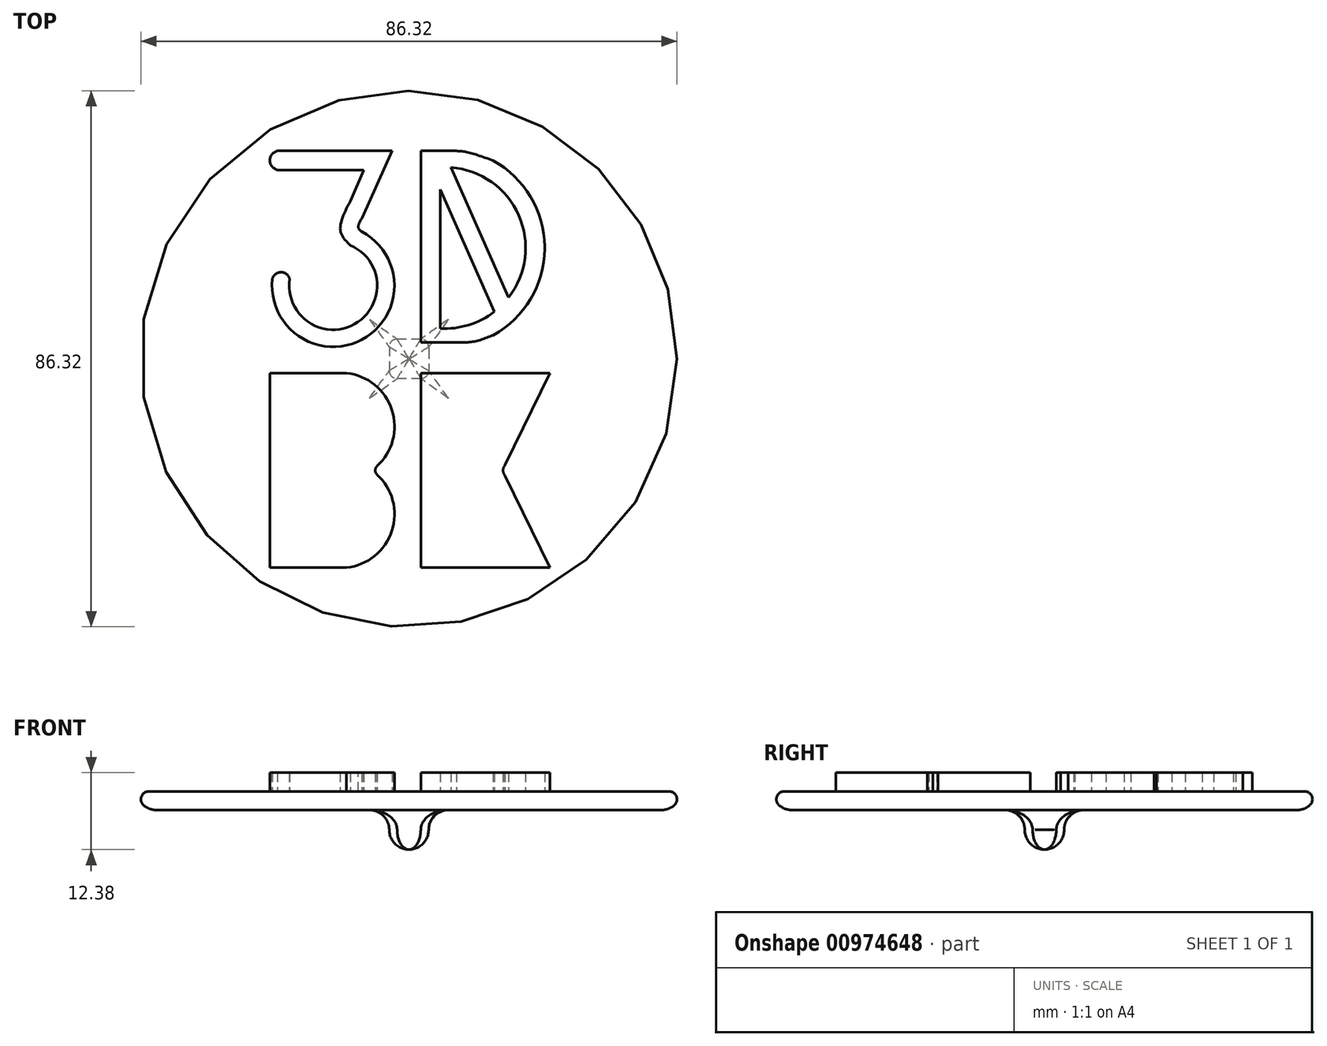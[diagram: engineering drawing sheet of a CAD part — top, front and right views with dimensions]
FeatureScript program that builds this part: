
annotation { "Feature Type Name" : "Feature", "Feature Type Description" : "" }
export const myFeature = defineFeature(function(context is Context, id is Id, definition is map)
    precondition{}
    {
        {
            var Q0;
            Q0=qCreatedBy(makeId("Top.planeOp"),FACE);
            var sketch = newSketch(context, id + "F0", { "sketchPlane" : qUnion([Q0])});
            skLineSegment(sketch, "E0", {"start": v(0, 56.35) * mm, "end": v(0, -56.35) * mm});
            skLineSegment(sketch, "E1", {"start": v(56.35, 0) * mm, "end": v(-56.35, 0) * mm});
            skPoint(sketch, "E2", {"position": v(0, 0) * mm});
            skPoint(sketch, "E3", {"position": v(-22.39, -33.62) * mm});
            skPoint(sketch, "E4", {"position": v(-22.39, 33.48) * mm});
            skPoint(sketch, "E5", {"position": v(21.85, 33.48) * mm});
            skLineSegment(sketch, "E6", {"start": v(1.95, 33.48) * mm, "end": v(7.67, 33.48) * mm});
            skLineSegment(sketch, "E7", {"start": v(21.85, -33.62) * mm, "end": v(1.95, -33.62) * mm});
            skLineSegment(sketch, "E8", {"start": v(21.85, 18.05) * mm, "end": v(21.85, 17.68) * mm});
            skLineSegment(sketch, "E9", {"start": v(-2.74, 33.48) * mm, "end": v(-21.16, 33.48) * mm});
            skLineSegment(sketch, "E10", {"start": v(-22.39, -33.62) * mm, "end": v(-10.07, -33.62) * mm});
            skLineSegment(sketch, "E11", {"start": v(-22.39, -2.3) * mm, "end": v(-22.39, -33.62) * mm});
            skPoint(sketch, "E12", {"position": v(-22.39, 31.95) * mm});
            skPoint(sketch, "E12.positionSnap0", {"position": v(-21.16, 31.95) * mm});
            skArc(sketch, "E13", {"start": v(-21.16, 33.48) * mm, "mid": v(-22.39, 31.95) * mm, "end": v(-21.16, 30.43) * mm});
            skPoint(sketch, "E14", {"position": v(-2.74, 33.48) * mm});
            skPoint(sketch, "E15", {"position": v(-7.3, 30.43) * mm});
            skLineSegment(sketch, "E16", {"start": v(-21.16, 30.43) * mm, "end": v(-7.3, 30.43) * mm});
            skPoint(sketch, "E17", {"position": v(-11.04, 20.68) * mm});
            skPoint(sketch, "E18", {"position": v(-9.45, 18.3) * mm});
            skPoint(sketch, "E19", {"position": v(-9.45, 25.39) * mm});
            skFitSpline(sketch, "E20", {"points": [v(-9.45, 25.39) * mm, v(-11.04, 20.68) * mm, v(-9.45, 18.3) * mm], "startDerivative": vector(-4.65, -9.06) * mm, "endDerivative": vector(5.1, -4.94) * mm});
            skLineSegment(sketch, "E21", {"start": v(-7.3, 30.43) * mm, "end": v(-9.45, 25.39) * mm});
            skPoint(sketch, "E22", {"position": v(-19.2, 12.85) * mm});
            skPoint(sketch, "E23", {"position": v(-12.14, 4.7) * mm});
            skArc(sketch, "E24", {"start": v(-19.2, 12.85) * mm, "mid": v(-8.74, 5.6) * mm, "end": v(-9.45, 18.3) * mm});
            skPoint(sketch, "E25", {"position": v(-8.14, 21.15) * mm});
            skPoint(sketch, "E26", {"position": v(-7.55, 20.43) * mm});
            skPoint(sketch, "E27", {"position": v(-7.55, 22.7) * mm});
            skFitSpline(sketch, "E28", {"points": [v(-7.55, 22.7) * mm, v(-8.14, 21.15) * mm, v(-7.55, 20.43) * mm], "startDerivative": vector(-1.74, -3) * mm, "endDerivative": vector(1.9, -1.47) * mm});
            skLineSegment(sketch, "E29", {"start": v(-2.74, 33.48) * mm, "end": v(-7.55, 22.7) * mm});
            skArc(sketch, "E30.0", {"start": v(-21.98, 12.85) * mm, "mid": v(-7.57, 3.08) * mm, "end": v(-7.62, 20.5) * mm});
            skPoint(sketch, "E31", {"position": v(-21.98, 12.85) * mm});
            skPoint(sketch, "E32", {"position": v(-20.63, 13.93) * mm});
            skArc(sketch, "E33", {"start": v(-19.2, 12.85) * mm, "mid": v(-20.59, 13.94) * mm, "end": v(-21.98, 12.85) * mm});
            skLineSegment(sketch, "E34", {"start": v(1.95, 33.48) * mm, "end": v(1.95, 2.25) * mm});
            skPoint(sketch, "E35", {"position": v(21.85, 18.05) * mm});
            skArc(sketch, "E36", {"start": v(13.56, 3.8) * mm, "mid": v(21.85, 17.87) * mm, "end": v(13.56, 31.93) * mm});
            skPoint(sketch, "E37", {"position": v(7.67, 33.48) * mm});
            skPoint(sketch, "E38", {"position": v(13.56, 31.93) * mm});
            skPoint(sketch, "E39", {"position": v(13.56, 3.8) * mm});
            skArc(sketch, "E40.0", {"start": v(5.03, 4.88) * mm, "mid": v(9.62, 5.44) * mm, "end": v(13.73, 7.58) * mm});
            skLineSegment(sketch, "E40.1", {"start": v(5.03, 27.26) * mm, "end": v(5.03, 4.88) * mm});
            skLineSegment(sketch, "E41", {"start": v(5.03, 27.26) * mm, "end": v(13.73, 7.58) * mm});
            skLineSegment(sketch, "E42", {"start": v(16.04, 9.89) * mm, "end": v(6.78, 30.83) * mm});
            skLineSegment(sketch, "E43", {"start": v(-22.39, -2.3) * mm, "end": v(-10.07, -2.3) * mm});
            skLineSegment(sketch, "E44", {"start": v(1.95, -2.3) * mm, "end": v(1.95, -33.62) * mm});
            skLineSegment(sketch, "E45", {"start": v(1.95, -2.3) * mm, "end": v(22.67, -2.3) * mm});
            skLineSegment(sketch, "E46", {"start": v(22.67, -2.3) * mm, "end": v(15.49, -17.1) * mm});
            skFitSpline(sketch, "E47", {"points": [v(15.49, -17.1) * mm, v(15.2, -17.6) * mm, v(15.17, -17.96) * mm], "startDerivative": vector(-0.63, -0.9) * mm, "endDerivative": vector(0.03, -0.82) * mm});
            skLineSegment(sketch, "E48.MirrorCS", {"start": v(1.95, -33.62) * mm, "end": v(22.67, -33.62) * mm});
            skLineSegment(sketch, "E49.MirrorCS", {"start": v(22.67, -33.62) * mm, "end": v(15.49, -18.82) * mm});
            skFitSpline(sketch, "E50.MirrorCS", {"points": [v(15.49, -18.82) * mm, v(15.2, -18.34) * mm, v(15.17, -17.96) * mm], "startDerivative": vector(-0.63, 0.9) * mm, "endDerivative": vector(0.03, 0.82) * mm});
            skArc(sketch, "E51", {"start": v(-5.17, -17.31) * mm, "mid": v(-2.75, -8.22) * mm, "end": v(-10.07, -2.3) * mm});
            skFitSpline(sketch, "E52", {"points": [v(-5.17, -17.31) * mm, v(-5.38, -17.68) * mm, v(-5.4, -17.96) * mm], "startDerivative": vector(-0.48, -0.68) * mm, "endDerivative": vector(0.02, -0.62) * mm});
            skArc(sketch, "E53.MirrorCS", {"start": v(-5.17, -18.61) * mm, "mid": v(-2.75, -27.7) * mm, "end": v(-10.07, -33.62) * mm});
            skFitSpline(sketch, "E54.MirrorCS", {"points": [v(-5.17, -18.61) * mm, v(-5.38, -18.25) * mm, v(-5.4, -17.96) * mm], "startDerivative": vector(-0.48, 0.68) * mm, "endDerivative": vector(0.02, 0.62) * mm});
            skPoint(sketch, "E55.end.orphan", {"position": v(-10.07, -33.62) * mm});
            skPoint(sketch, "E56.orphan", {"position": v(-10.07, -17.96) * mm});
            skPoint(sketch, "E57.orphan", {"position": v(0, -33.62) * mm});
            skLineSegment(sketch, "E58.MirrorCS", {"start": v(0, 2.62) * mm, "end": v(7.67, 2.62) * mm});
            skArc(sketch, "E59.trimOffspring", {"start": v(16.04, 9.89) * mm, "mid": v(17.67, 23.12) * mm, "end": v(6.78, 30.83) * mm});
            skPoint(sketch, "E60", {"position": v(7.67, 2.62) * mm});
            skFitSpline(sketch, "E61", {"points": [v(13.56, 3.8) * mm, v(10.55, 2.81) * mm, v(7.67, 2.62) * mm], "startDerivative": vector(-5.9, -2.33) * mm, "endDerivative": vector(-5.9, -0.02) * mm});
            skPoint(sketch, "E62.1.internal.snap0", {"position": v(9.38, 17.42) * mm});
            skFitSpline(sketch, "E62", {"points": [v(13.56, 31.93) * mm, v(9.38, 33.27) * mm, v(7.67, 33.48) * mm], "startDerivative": vector(-7.54, 2.7) * mm, "endDerivative": vector(-3.99, 0.22) * mm});
            skPoint(sketch, "E63.orphan", {"position": v(10.87, 2.62) * mm});
            skPoint(sketch, "E64.orphan", {"position": v(0, 33.48) * mm});
            skPoint(sketch, "E65.trimOffspring.start.orphan", {"position": v(21.85, 2.62) * mm});
            skLineSegment(sketch, "E66", {"start": v(-27.8, 0) * mm, "end": v(-27.8, 46.45) * mm});
            skLineSegment(sketch, "E67", {"start": v(-27.8, 46.45) * mm, "end": v(0, 46.45) * mm});
            skLineSegment(sketch, "E68.MirrorCS", {"start": v(27.8, 0) * mm, "end": v(27.8, 46.45) * mm});
            skLineSegment(sketch, "E69.MirrorCS", {"start": v(-27.8, -46.45) * mm, "end": v(0, -46.45) * mm});
            skLineSegment(sketch, "E70.MirrorCS", {"start": v(-27.8, 0) * mm, "end": v(-27.8, -46.45) * mm});
            skLineSegment(sketch, "E71.MirrorCS", {"start": v(27.8, 46.45) * mm, "end": v(0, 46.45) * mm});
            skLineSegment(sketch, "E72.MirrorCS", {"start": v(27.8, 0) * mm, "end": v(27.8, -46.45) * mm});
            skLineSegment(sketch, "E73.MirrorCS", {"start": v(27.8, -46.45) * mm, "end": v(0, -46.45) * mm});
            skSolve(sketch);
        }
        {
            var Q0;
            Q0=qCreatedBy(makeId("Top.planeOp"),FACE);
            var sketch = newSketch(context, id + "F1", { "sketchPlane" : qUnion([Q0])});
            skCircle(sketch, "E74", {"center": v(0, 0) * mm, "radius": 43.82 * mm});
            skSolve(sketch);
        }
        {
            var Q0;
            Q0 = qSketchRegion(id + "F1", true);
            extrude(context, id + "F2", {"entities" : qUnion([Q0]), "oppositeDirection" : true, "depth" : 3 * mm, "offsetDistance" : 25.4 * mm});
        }
        {
            var Q0;
            Q0=makeQuery(id+"F0.imprint","IMPRINT",FACE,{"disambiguationData":[TD([[makeQuery(id+"F0.imprint","IMPRINT",EDGE,{"derivedFrom":sQuery(id+"F0.wireOp",EDGE,"E10")}),1.0]])]});
            var Q1;
            {var subQ0=sQuery(id+"F0.wireOp",EDGE,"E44");Q1=makeQuery(id+"F0.imprint","IMPRINT",FACE,{"disambiguationData":[TD([[makeQuery(id+"F0.imprint","IMPRINT",EDGE,{"derivedFrom":subQ0}),1.0]])]});}
            var Q2;
            Q2=makeQuery(id+"F0.imprint","IMPRINT",FACE,{"disambiguationData":[TD([[makeQuery(id+"F0.imprint","IMPRINT",EDGE,{"derivedFrom":sQuery(id+"F0.wireOp",EDGE,"E9")}),1.0]])]});
            var Q3;
            {var subQ7=sQuery(id+"F0.wireOp",EDGE,"E6");Q3=makeQuery(id+"F0.imprint","IMPRINT",FACE,{"disambiguationData":[TD([[makeQuery(id+"F0.imprint","IMPRINT",EDGE,{"derivedFrom":subQ7}),-1.0]])]});}
            extrude(context, id + "F3", {"entities" : qUnion([Q0, Q1, Q2, Q3]), "operationType" : NewBodyOperationType.ADD, "depth" : 3 * mm, "offsetDistance" : 25.4 * mm});
        }
        {
            var Q0;
            Q0=makeQuery(id+"F2.opExtrude","CAP_FACE",FACE,{"disambiguationData":[OSD([sQuery(id+"F1.wireOp",EDGE,"E74")])],"isStart":false});
            var sketch = newSketch(context, id + "F4", { "sketchPlane" : qUnion([Q0])});
            skLineSegment(sketch, "E75.bottom", {"start": v(3.18, -3.17) * mm, "end": v(-3.18, -3.18) * mm});
            skLineSegment(sketch, "E75.top", {"start": v(3.18, 3.18) * mm, "end": v(-3.18, 3.17) * mm});
            skLineSegment(sketch, "E75.left", {"start": v(3.18, -3.17) * mm, "end": v(3.18, 3.18) * mm});
            skLineSegment(sketch, "E75.right", {"start": v(-3.18, -3.18) * mm, "end": v(-3.18, 3.17) * mm});
            skPoint(sketch, "E75.middle", {"position": v(0, 0) * mm});
            skSolve(sketch);
        }
        {
            var Q0;
            Q0 = qSketchRegion(id + "F4", true);
            extrude(context, id + "F5", {"entities" : qUnion([Q0]), "operationType" : NewBodyOperationType.ADD, "depth" : 6.38 * mm, "offsetDistance" : 25.4 * mm});
        }
        {
            var Q0;
            Q0=makeQuery(id+"F5.opExtrude","CAP_EDGE",EDGE,{"disambiguationData":[OSD([sQuery(id+"F4.wireOp",EDGE,"E75.right")])],"isStart":false});
            var Q1;
            Q1=makeQuery(id+"F5.opExtrude","CAP_EDGE",EDGE,{"disambiguationData":[OSD([sQuery(id+"F4.wireOp",EDGE,"E75.top")])],"isStart":false});
            var Q2;
            Q2=makeQuery(id+"F5.opExtrude","CAP_EDGE",EDGE,{"disambiguationData":[OSD([sQuery(id+"F4.wireOp",EDGE,"E75.left")])],"isStart":false});
            var Q3;
            Q3=makeQuery(id+"F5.opExtrude","CAP_EDGE",EDGE,{"disambiguationData":[OSD([sQuery(id+"F4.wireOp",EDGE,"E75.bottom")])],"isStart":false});
            var Q4;
            Q4=makeQuery(id+"F5.opExtrude","CAP_EDGE",EDGE,{"disambiguationData":[OSD([sQuery(id+"F4.wireOp",EDGE,"E75.right")])],"isStart":true});
            var Q5;
            Q5=makeQuery(id+"F5.opExtrude","CAP_EDGE",EDGE,{"disambiguationData":[OSD([sQuery(id+"F4.wireOp",EDGE,"E75.top")])],"isStart":true});
            var Q6;
            Q6=makeQuery(id+"F5.opExtrude","CAP_EDGE",EDGE,{"disambiguationData":[OSD([sQuery(id+"F4.wireOp",EDGE,"E75.bottom")])],"isStart":true});
            var Q7;
            Q7=makeQuery(id+"F5.opExtrude","CAP_EDGE",EDGE,{"disambiguationData":[OSD([sQuery(id+"F4.wireOp",EDGE,"E75.left")])],"isStart":true});
            var Q8;
            Q8=makeQuery(id+"F2.opExtrude","CAP_FACE",FACE,{"disambiguationData":[OSD([sQuery(id+"F1.wireOp",EDGE,"E74")])],"isStart":false});
            fillet(context, id + "F6", {"entities" : qUnion([Q0, Q1, Q2, Q3, Q4, Q5, Q6, Q7, Q8]), "radius" : 3.17 * mm, "tangentPropagation" : true, "allowEdgeOverflow" : false});
        }
        {
            var Q0;
            Q0=makeQuery(id+"F5.opExtrude","SWEPT_FACE",FACE,{"disambiguationData":[OSD([sQuery(id+"F4.wireOp",EDGE,"E75.left")])]});
            extrude(context, id + "F7", {"entities" : qUnion([Q0]), "operationType" : NewBodyOperationType.ADD, "depth" : 25.4 * mm, "offsetDistance" : 25.4 * mm});
        }
        {
            var Q0;
            Q0=makeQuery(id+"F7.opExtrude","CAP_FACE",FACE,{"disambiguationData":[OSD([sQuery(id+"F4.wireOp",EDGE,"E75.left")])],"isStart":false});
            var sketch = newSketch(context, id + "F8", { "sketchPlane" : qUnion([Q0])});
            skCircle(sketch, "E76", {"center": v(0, -6.19) * mm, "radius": 1.5 * mm});
            skPoint(sketch, "E76.centerSnap0", {"position": v(3.17, -6.19) * mm});
            skPoint(sketch, "E76.centerSnap1", {"position": v(0, -6.2) * mm});
            skSolve(sketch);
        }
        {
            var Q0;
            {var subQ0=sQuery(id+"F8.wireOp",EDGE,"E76");var subQ1=sQuery(id+"F4.wireOp",EDGE,"E75.left");var subQ2=makeQuery(id+"F7.opExtrude","CAP_EDGE",EDGE,{"disambiguationData":[OSD([subQ1]),TDD([makeQuery(id+"F6.opFillet","BLEND_EDGE",EDGE,{"blendedFrom":[makeQuery(id+"F5.opExtrude","CAP_EDGE",EDGE,{"disambiguationData":[OSD([subQ1])],"isStart":true}),makeQuery(id+"F5.opExtrude","SWEPT_FACE",FACE,{"disambiguationData":[OSD([subQ1])]})],"blendedInto":[makeQuery(id+"F5.opExtrude","SWEPT_FACE",FACE,{"disambiguationData":[OSD([subQ1])]})]})])],"isStart":false});var subQ3=makeQuery(id+"F8.imprint","INTERSECT",VERTEX,{"disambiguationData":[OD(0.0)],"derivedFrom":[subQ2,subQ0]});Q0=makeQuery(id+"F8.imprint","IMPRINT",FACE,{"disambiguationData":[TD([[makeQuery(id+"F8.imprint","IMPRINT",EDGE,{"disambiguationData":[TD([[subQ3,1.0]])],"derivedFrom":subQ0}),1.0]])]});}
            var Q1;
            {var subQ0=sQuery(id+"F8.wireOp",EDGE,"E76");var subQ1=sQuery(id+"F4.wireOp",EDGE,"E75.left");var subQ2=makeQuery(id+"F7.opExtrude","CAP_EDGE",EDGE,{"disambiguationData":[OSD([subQ1]),TDD([makeQuery(id+"F6.opFillet","BLEND_EDGE",EDGE,{"blendedFrom":[makeQuery(id+"F5.opExtrude","CAP_EDGE",EDGE,{"disambiguationData":[OSD([subQ1])],"isStart":false}),makeQuery(id+"F5.opExtrude","SWEPT_FACE",FACE,{"disambiguationData":[OSD([subQ1])]})],"blendedInto":[makeQuery(id+"F5.opExtrude","SWEPT_FACE",FACE,{"disambiguationData":[OSD([subQ1])]})]})])],"isStart":false});var subQ3=makeQuery(id+"F8.imprint","INTERSECT",VERTEX,{"disambiguationData":[OD(0.0)],"derivedFrom":[subQ2,subQ0]});Q1=makeQuery(id+"F8.imprint","IMPRINT",FACE,{"disambiguationData":[TD([[makeQuery(id+"F8.imprint","IMPRINT",EDGE,{"disambiguationData":[TD([[subQ3,-1.0]])],"derivedFrom":subQ0}),1.0]])]});}
            var Q2;
            {var subQ0=sQuery(id+"F8.wireOp",EDGE,"E76");var subQ1=sQuery(id+"F4.wireOp",EDGE,"E75.left");var subQ2=makeQuery(id+"F5.opExtrude","SWEPT_FACE",FACE,{"disambiguationData":[OSD([subQ1])]});var subQ3=makeQuery(id+"F7.opExtrude","CAP_EDGE",EDGE,{"disambiguationData":[OSD([subQ1]),TDD([makeQuery(id+"F6.opFillet","BLEND_EDGE",EDGE,{"blendedFrom":[makeQuery(id+"F5.opExtrude","CAP_EDGE",EDGE,{"disambiguationData":[OSD([subQ1])],"isStart":true}),subQ2],"blendedInto":[subQ2]})])],"isStart":false});var subQ4=makeQuery(id+"F8.imprint","INTERSECT",VERTEX,{"disambiguationData":[OD(0.0)],"derivedFrom":[subQ3,subQ0]});Q2=makeQuery(id+"F8.imprint","IMPRINT",FACE,{"disambiguationData":[TD([[makeQuery(id+"F8.imprint","IMPRINT",EDGE,{"disambiguationData":[TD([[subQ4,-1.0]])],"derivedFrom":subQ0}),1.0]])]});}
            var Q3;
            {var subQ0=sQuery(id+"F4.wireOp",EDGE,"E75.right");Q3=makeQuery(id+"F6.opFillet","BLEND_FACE",FACE,{"disambiguationData":[OSD([subQ0]),TDD([makeQuery(id+"F5.opExtrude","CAP_EDGE",EDGE,{"disambiguationData":[OSD([subQ0])],"isStart":true})])]});}
            extrude(context, id + "F9", {"entities" : qUnion([Q0, Q1, Q2]), "operationType" : NewBodyOperationType.REMOVE, "endBound" : BoundingType.UP_TO_SURFACE, "oppositeDirection" : true, "depth" : 25.4 * mm, "endBoundEntityFace" : qUnion([Q3]), "offsetDistance" : 25.4 * mm});
        }
        {
            var Q0;
            {var subQ0=sQuery(id+"F4.wireOp",EDGE,"E75.left");var subQ2=sQuery(id+"F4.wireOp",EDGE,"E75.top");Q0=makeQuery(id+"F9.boolean.opBoolean","SPLIT",FACE,{"disambiguationData":[TD([makeQuery(id+"F5.opExtrude","SWEPT_FACE",FACE,{"disambiguationData":[OSD([subQ2])]})])],"derivedFrom":makeQuery(id+"F7.opExtrude","CAP_FACE",FACE,{"disambiguationData":[OSD([subQ0])],"isStart":false})});}
            var Q1;
            {var subQ0=sQuery(id+"F4.wireOp",EDGE,"E75.left");var subQ2=sQuery(id+"F4.wireOp",EDGE,"E75.bottom");Q1=makeQuery(id+"F9.boolean.opBoolean","SPLIT",FACE,{"disambiguationData":[TD([makeQuery(id+"F5.opExtrude","SWEPT_FACE",FACE,{"disambiguationData":[OSD([subQ2])]})])],"derivedFrom":makeQuery(id+"F7.opExtrude","CAP_FACE",FACE,{"disambiguationData":[OSD([subQ0])],"isStart":false})});}
            extrude(context, id + "F10", {"entities" : qUnion([Q0, Q1]), "operationType" : NewBodyOperationType.REMOVE, "oppositeDirection" : true, "depth" : 25.4 * mm, "offsetDistance" : 25.4 * mm});
        }
        {
            var Q0;
            {var subQ3=sQuery(id+"F1.wireOp",EDGE,"E74");Q0=makeQuery(id+"F6.opFillet","BLEND_EDGE",EDGE,{"blendedFrom":[makeQuery(id+"F2.opExtrude","CAP_EDGE",EDGE,{"disambiguationData":[OSD([subQ3])],"isStart":false}),makeQuery(id+"F3.boolean.opBoolean","SPLIT",FACE,{"disambiguationData":[TD([makeQuery(id+"F2.opExtrude","SWEPT_FACE",FACE,{"disambiguationData":[OSD([subQ3])]})])],"derivedFrom":makeQuery(id+"F2.opExtrude","CAP_FACE",FACE,{"disambiguationData":[OSD([subQ3])],"isStart":true})})],"blendedInto":[makeQuery(id+"F3.boolean.opBoolean","SPLIT",FACE,{"disambiguationData":[TD([makeQuery(id+"F2.opExtrude","SWEPT_FACE",FACE,{"disambiguationData":[OSD([subQ3])]})])],"derivedFrom":makeQuery(id+"F2.opExtrude","CAP_FACE",FACE,{"disambiguationData":[OSD([subQ3])],"isStart":true})})]});}
            fillet(context, id + "F11", {"entities" : qUnion([Q0]), "radius" : 1.27 * mm, "tangentPropagation" : true, "allowEdgeOverflow" : false});
        }
        {
            var Q0;
            Q0=makeQuery(id+"F6.opFillet","BLEND_EDGE",EDGE,{"blendedFrom":[makeQuery(id+"F5.opExtrude","CAP_EDGE",EDGE,{"disambiguationData":[OSD([sQuery(id+"F4.wireOp",EDGE,"E75.top")])],"isStart":false}),makeQuery(id+"F5.opExtrude","CAP_EDGE",EDGE,{"disambiguationData":[OSD([sQuery(id+"F4.wireOp",EDGE,"E75.left")])],"isStart":false})],"blendedInto":[]});
            var Q1;
            Q1=makeQuery(id+"F6.opFillet","BLEND_EDGE",EDGE,{"blendedFrom":[makeQuery(id+"F5.opExtrude","CAP_EDGE",EDGE,{"disambiguationData":[OSD([sQuery(id+"F4.wireOp",EDGE,"E75.bottom")])],"isStart":false}),makeQuery(id+"F5.opExtrude","CAP_EDGE",EDGE,{"disambiguationData":[OSD([sQuery(id+"F4.wireOp",EDGE,"E75.left")])],"isStart":false})],"blendedInto":[]});
            var Q2;
            Q2=makeQuery(id+"F6.opFillet","BLEND_EDGE",EDGE,{"blendedFrom":[makeQuery(id+"F5.opExtrude","CAP_EDGE",EDGE,{"disambiguationData":[OSD([sQuery(id+"F4.wireOp",EDGE,"E75.bottom")])],"isStart":false}),makeQuery(id+"F5.opExtrude","CAP_EDGE",EDGE,{"disambiguationData":[OSD([sQuery(id+"F4.wireOp",EDGE,"E75.right")])],"isStart":false})],"blendedInto":[]});
            var Q3;
            Q3=makeQuery(id+"F6.opFillet","BLEND_EDGE",EDGE,{"blendedFrom":[makeQuery(id+"F5.opExtrude","CAP_EDGE",EDGE,{"disambiguationData":[OSD([sQuery(id+"F4.wireOp",EDGE,"E75.top")])],"isStart":false}),makeQuery(id+"F5.opExtrude","CAP_EDGE",EDGE,{"disambiguationData":[OSD([sQuery(id+"F4.wireOp",EDGE,"E75.right")])],"isStart":false})],"blendedInto":[]});
            var Q4;
            Q4=makeQuery(id+"F2.opExtrude","CAP_FACE",FACE,{"disambiguationData":[OSD([sQuery(id+"F1.wireOp",EDGE,"E74")])],"isStart":false});
            fillet(context, id + "F12", {"entities" : qUnion([Q0, Q1, Q2, Q3, Q4]), "radius" : 1.27 * mm, "tangentPropagation" : true, "allowEdgeOverflow" : false});
        }
    });
